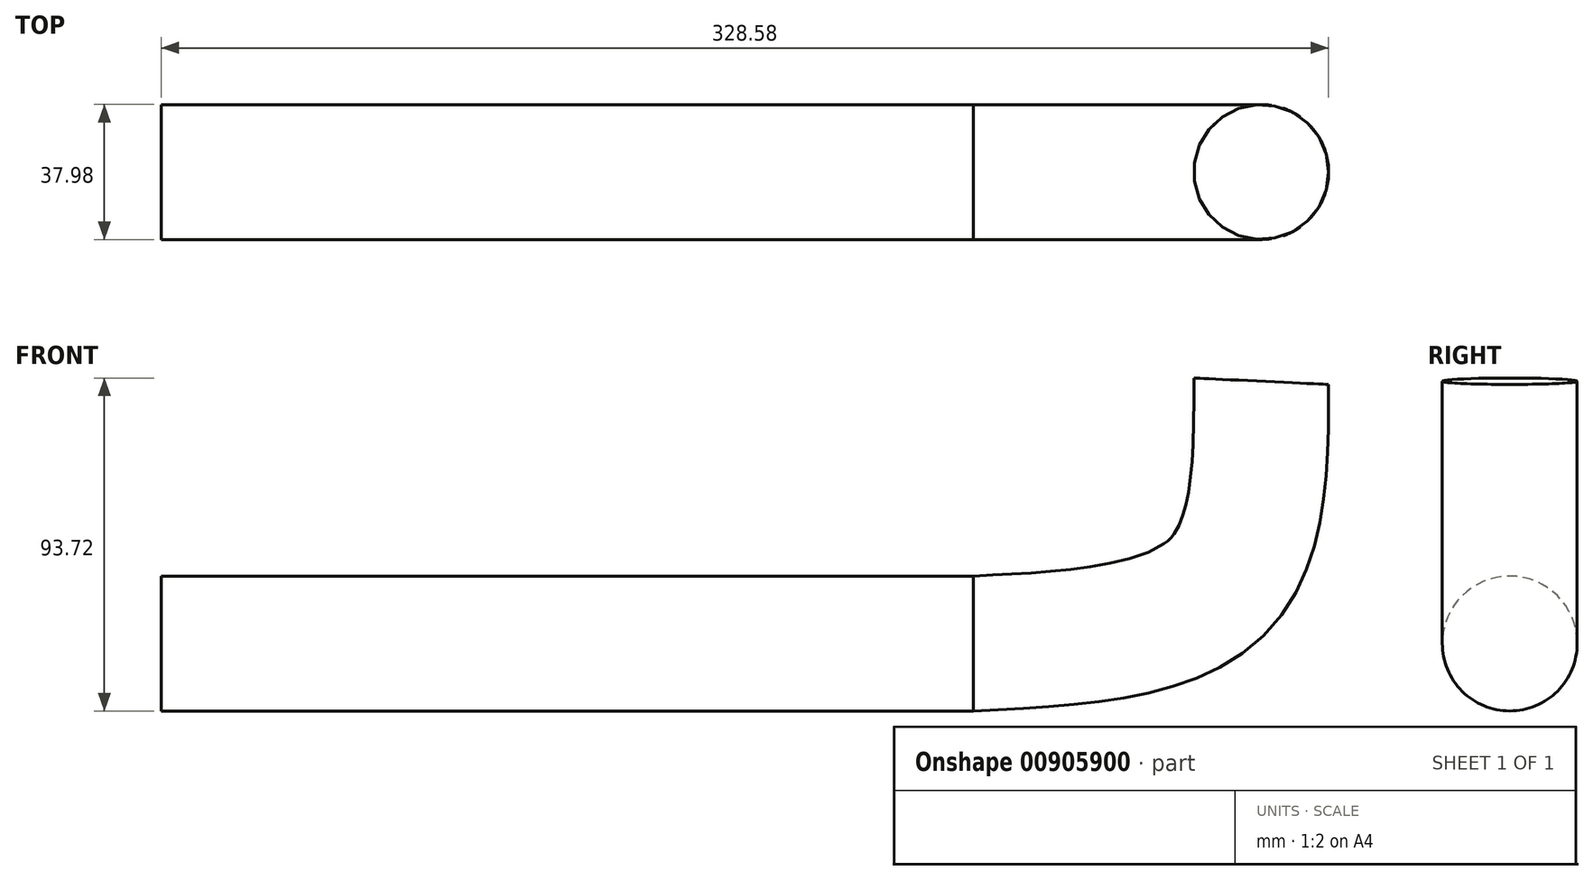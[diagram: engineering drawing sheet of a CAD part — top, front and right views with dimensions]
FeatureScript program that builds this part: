
annotation { "Feature Type Name" : "Feature", "Feature Type Description" : "" }
export const myFeature = defineFeature(function(context is Context, id is Id, definition is map)
    precondition{}
    {
        {
            var Q0;
            Q0=qCreatedBy(makeId("Right.planeOp"),FACE);
            var sketch = newSketch(context, id + "F0", { "sketchPlane" : qUnion([Q0])});
            skCircle(sketch, "E0", {"center": v(0, 0) * mm, "radius": 18.99 * mm});
            skSolve(sketch);
        }
        {
            var Q0;
            Q0=qCreatedBy(makeId("Front.planeOp"),FACE);
            var sketch = newSketch(context, id + "F1", { "sketchPlane" : qUnion([Q0])});
            skFitSpline(sketch, "E1", {"points": [v(0, 0) * mm, v(68.93, 16.26) * mm, v(81.02, 73.82) * mm], "startDerivative": vector(159.58, 7.63) * mm, "endDerivative": vector(-0.01, 142.1) * mm});
            skSolve(sketch);
        }
        {
            var Q0;
            Q0 = qSketchRegion(id + "F0", true);
            var Q1;
            Q1 = qConstructionFilter(qBodyType(qCreatedBy(id + "F1" ,EDGE), BodyType.WIRE), ConstructionObject.NO);
            sweep(context, id + "F2", {"profiles" : qUnion([Q0]), "path" : qUnion([Q1])});
        }
        {
            var Q0;
            Q0=makeQuery(id+"F2.opSweep","CAP_FACE",FACE,{"disambiguationData":[OSD([sQuery(id+"F0.wireOp",EDGE,"E0"),sQuery(id+"F1.wireOp",VERTEX,"E1.start")])],"isStart":true});
            var sketch = newSketch(context, id + "F3", { "sketchPlane" : qUnion([Q0])});
            skCircle(sketch, "E2", {"center": v(0, 0) * mm, "radius": 18.99 * mm});
            skSolve(sketch);
        }
        {
            var Q0;
            Q0 = qSketchRegion(id + "F3", true);
            extrude(context, id + "F4", {"entities" : qUnion([Q0]), "operationType" : NewBodyOperationType.ADD, "depth" : 228.6 * mm, "offsetDistance" : 25.4 * mm});
        }
    });
